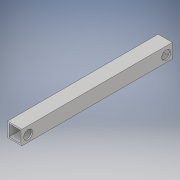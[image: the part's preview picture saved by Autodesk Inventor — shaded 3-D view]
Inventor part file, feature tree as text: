
AUTODESK INVENTOR PART (.ipt)
format: ipt  version: 2018 (Build 220112000, 112)  size: 113,664 bytes
history: native  units: in
note: dims shown in document units (in); Inventor stores cm internally (conversion verified against a paired STEP export)
features: extrude x2, sketch x2
ambient origin geometry x8: Origin, YZ Plane, XZ Plane, XY Plane, X Axis, Y Axis, Z Axis, Center Point
bodies: Solid1 (feature_tree)
feature tree (4):
  extrude  "Extrusion1"  Depth=1.0in
  extrude  "Extrusion2"  Depth=0.1in
  sketch  "Sketch1"  dims[d0=1.0in d1=1.0in]
  sketch  "Sketch2"  dims[d2=0.1in d3=0.1in d4=10.5in d5=0.0in d6=9.626in d7=0.625in d8=0.625in d9=0.437in d10=0.437in d11=0.1in d12=0.0in]
